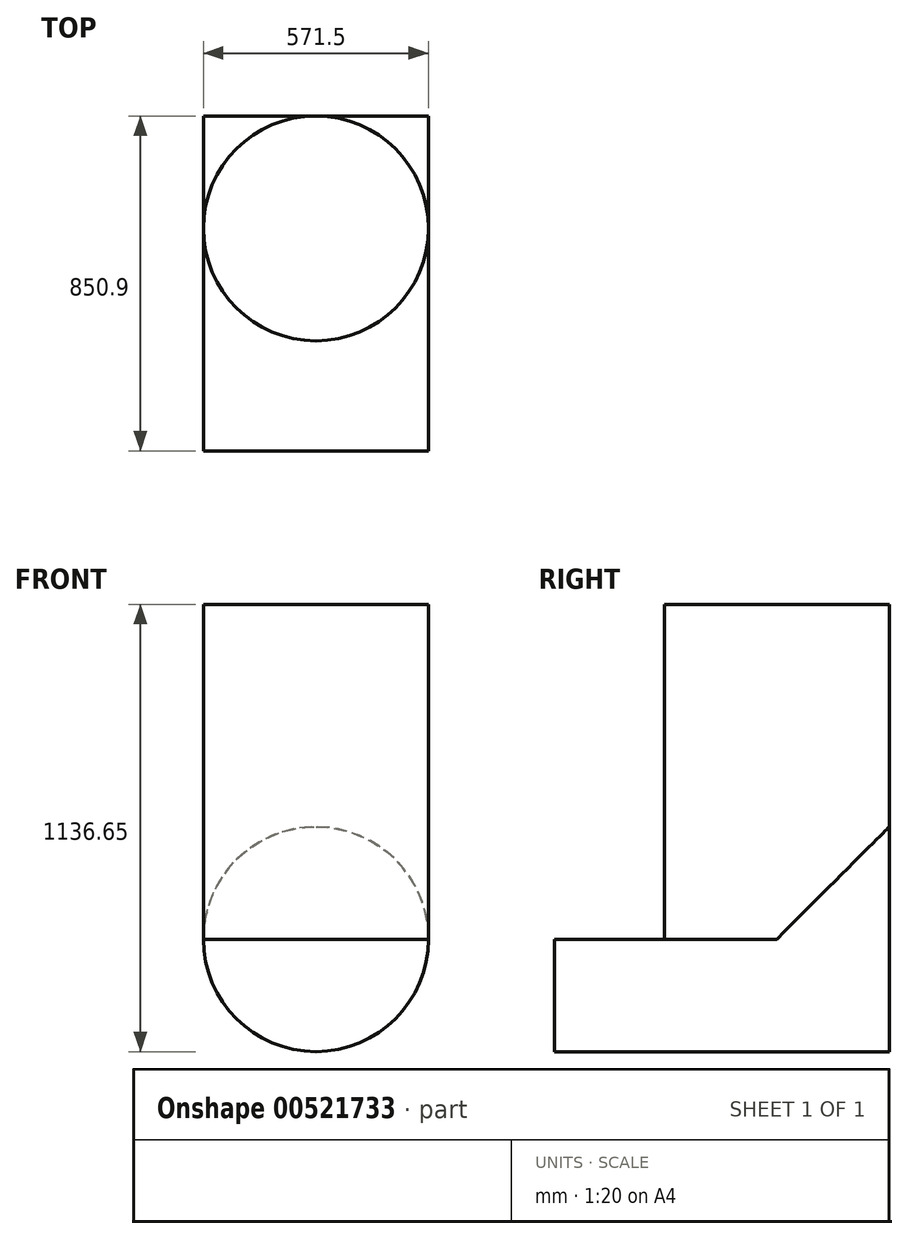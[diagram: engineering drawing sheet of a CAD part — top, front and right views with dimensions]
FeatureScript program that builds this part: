
annotation { "Feature Type Name" : "Feature", "Feature Type Description" : "" }
export const myFeature = defineFeature(function(context is Context, id is Id, definition is map)
    precondition{}
    {
        {
            var Q0;
            Q0=qCreatedBy(makeId("Top.planeOp"),FACE);
            var sketch = newSketch(context, id + "F0", { "sketchPlane" : qUnion([Q0])});
            skCircle(sketch, "E0", {"center": v(0, 0) * mm, "radius": 285.75 * mm});
            skSolve(sketch);
        }
        {
            var Q0;
            Q0 = qSketchRegion(id + "F0", true);
            extrude(context, id + "F1", {"entities" : qUnion([Q0]), "depth" : 850.9 * mm, "offsetDistance" : 25.4 * mm});
        }
        {
            var Q0;
            Q0=qCreatedBy(makeId("Front.planeOp"),FACE);
            var sketch = newSketch(context, id + "F2", { "sketchPlane" : qUnion([Q0])});
            skCircle(sketch, "E1", {"center": v(0, 0) * mm, "radius": 285.75 * mm});
            skSolve(sketch);
        }
        {
            var Q0;
            Q0 = qSketchRegion(id + "F2", true);
            extrude(context, id + "F3", {"entities" : qUnion([Q0]), "operationType" : NewBodyOperationType.ADD, "oppositeDirection" : true, "depth" : 285.75 * mm, "offsetDistance" : 25.4 * mm});
        }
        {
            var Q0;
            Q0=makeQuery(id+"F3.opExtrude","CAP_FACE",FACE,{"disambiguationData":[OSD([sQuery(id+"F2.wireOp",EDGE,"E1")])],"isStart":true});
            extrude(context, id + "F4", {"entities" : qUnion([Q0]), "operationType" : NewBodyOperationType.ADD, "depth" : 565.15 * mm, "offsetDistance" : 25.4 * mm});
        }
    });
